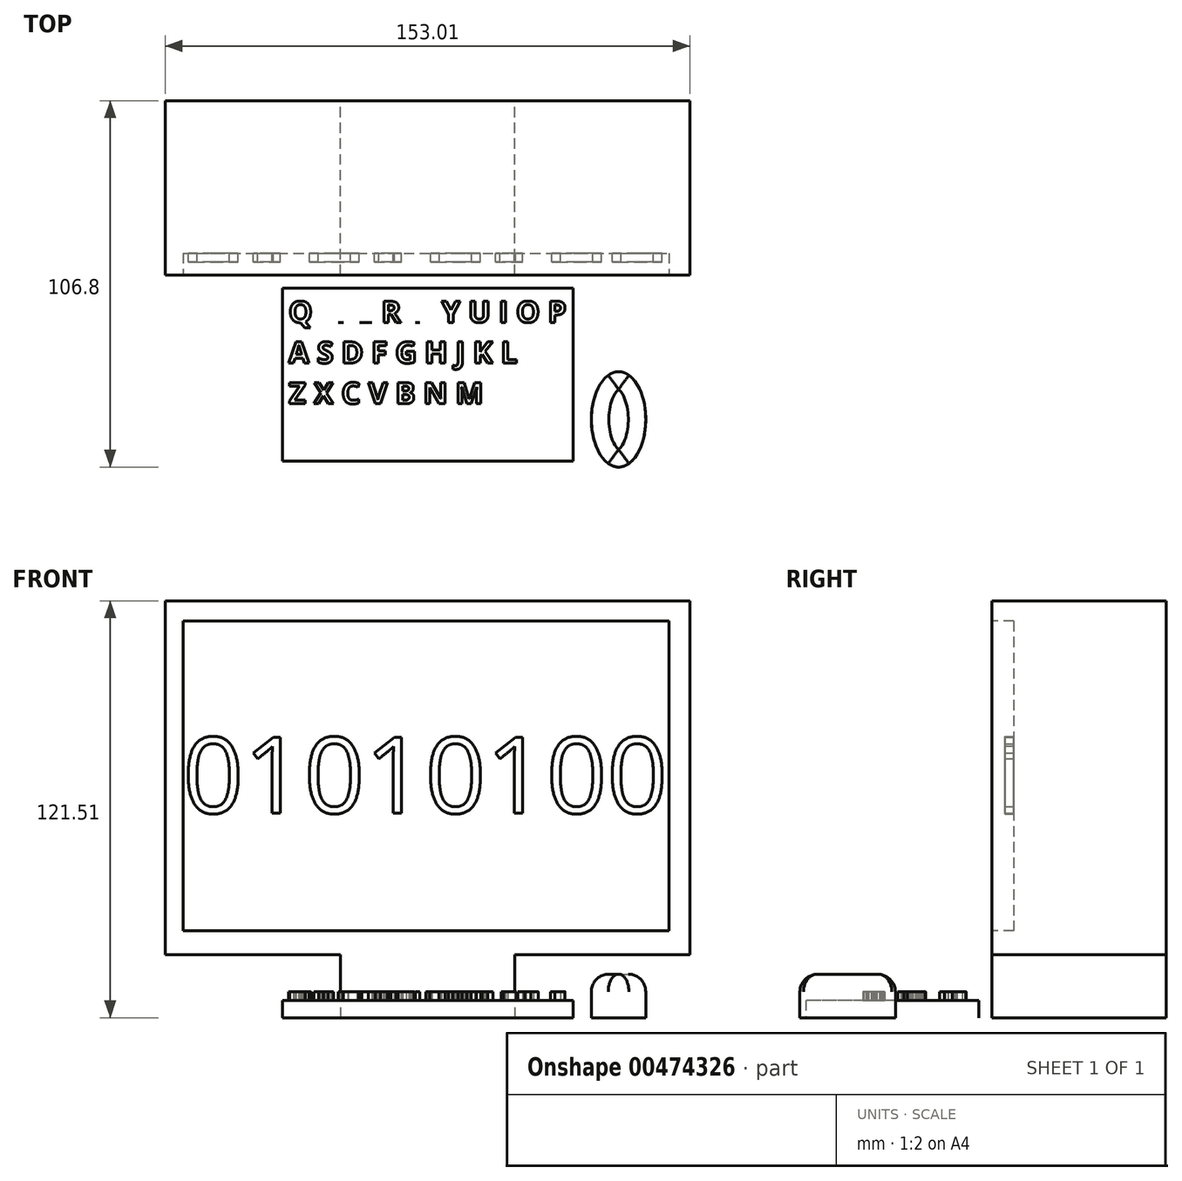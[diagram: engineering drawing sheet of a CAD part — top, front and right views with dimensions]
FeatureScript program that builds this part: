
annotation { "Feature Type Name" : "Feature", "Feature Type Description" : "" }
export const myFeature = defineFeature(function(context is Context, id is Id, definition is map)
    precondition{}
    {
        {
            var Q0;
            Q0=qCreatedBy(makeId("Top.planeOp"),FACE);
            var sketch = newSketch(context, id + "F0", { "sketchPlane" : qUnion([Q0])});
            skLineSegment(sketch, "E0.bottom", {"start": v(25.4, -25.4) * mm, "end": v(-25.4, -25.4) * mm});
            skLineSegment(sketch, "E0.top", {"start": v(25.4, 25.4) * mm, "end": v(-25.4, 25.4) * mm});
            skLineSegment(sketch, "E0.left", {"start": v(25.4, -25.4) * mm, "end": v(25.4, 25.4) * mm});
            skLineSegment(sketch, "E0.right", {"start": v(-25.4, -25.4) * mm, "end": v(-25.4, 25.4) * mm});
            skPoint(sketch, "E0.middle", {"position": v(0, 0) * mm});
            skSolve(sketch);
        }
        {
            var Q0;
            Q0=qSketchRegion(id+"F0",true);
            extrude(context, id + "F1", {"entities" : qUnion([Q0]), "depth" : 25.4 * mm});
        }
        {
            var Q0;
            Q0=qCreatedBy(makeId("Front.planeOp"),FACE);
            var sketch = newSketch(context, id + "F2", { "sketchPlane" : qUnion([Q0])});
            skLineSegment(sketch, "E1.bottom", {"start": v(-76.56, 18.4) * mm, "end": v(76.45, 18.4) * mm});
            skLineSegment(sketch, "E1.top", {"start": v(-76.56, 121.5) * mm, "end": v(76.45, 121.5) * mm});
            skLineSegment(sketch, "E1.left", {"start": v(-76.56, 18.4) * mm, "end": v(-76.56, 121.5) * mm});
            skLineSegment(sketch, "E1.right", {"start": v(76.45, 18.4) * mm, "end": v(76.45, 121.5) * mm});
            skSolve(sketch);
        }
        {
            var Q0;
            Q0=makeQuery(id+"F2.imprint","IMPRINT",FACE,{"disambiguationData":[TD([[makeQuery(id+"F2.imprint","IMPRINT",EDGE,{"derivedFrom":sQuery(id+"F2.wireOp",EDGE,"E1.bottom")}),1.0]])]});
            extrude(context, id + "F3", {"entities" : qUnion([Q0]), "operationType" : NewBodyOperationType.ADD, "depth" : 25.4 * mm});
        }
        {
            var Q0;
            Q0=makeQuery(id+"F3.opExtrude","CAP_FACE",FACE,{"disambiguationData":[OSD([sQuery(id+"F2.wireOp",EDGE,"E1.bottom"),sQuery(id+"F2.wireOp",EDGE,"E1.top"),sQuery(id+"F2.wireOp",EDGE,"E1.left"),sQuery(id+"F2.wireOp",EDGE,"E1.right")])],"isStart":true});
            extrude(context, id + "F4", {"entities" : qUnion([Q0]), "operationType" : NewBodyOperationType.ADD, "depth" : 25.4 * mm});
        }
        {
            var Q0;
            Q0=makeQuery(id+"F3.boolean.opBoolean","MERGE",FACE,{"derivedFrom":[makeQuery(id+"F1.opExtrude","SWEPT_FACE",FACE,{"disambiguationData":[OSD([sQuery(id+"F0.wireOp",EDGE,"E0.bottom")])]}),makeQuery(id+"F3.opExtrude","CAP_FACE",FACE,{"disambiguationData":[OSD([sQuery(id+"F2.wireOp",EDGE,"E1.bottom"),sQuery(id+"F2.wireOp",EDGE,"E1.top"),sQuery(id+"F2.wireOp",EDGE,"E1.left"),sQuery(id+"F2.wireOp",EDGE,"E1.right")])],"isStart":false})]});
            var sketch = newSketch(context, id + "F5", { "sketchPlane" : qUnion([Q0])});
            skLineSegment(sketch, "E2.bottom", {"start": v(-71.36, 115.62) * mm, "end": v(70.34, 115.62) * mm});
            skLineSegment(sketch, "E2.top", {"start": v(-71.36, 25.36) * mm, "end": v(70.34, 25.36) * mm});
            skLineSegment(sketch, "E2.left", {"start": v(-71.36, 115.62) * mm, "end": v(-71.36, 25.36) * mm});
            skLineSegment(sketch, "E2.right", {"start": v(70.34, 115.62) * mm, "end": v(70.34, 25.36) * mm});
            skSolve(sketch);
        }
        {
            var Q0;
            Q0=makeQuery(id+"F5.imprint","IMPRINT",FACE,{"disambiguationData":[TD([[makeQuery(id+"F5.imprint","IMPRINT",EDGE,{"derivedFrom":sQuery(id+"F5.wireOp",EDGE,"E2.bottom")}),-1.0]])]});
            extrude(context, id + "F6", {"entities" : qUnion([Q0]), "operationType" : NewBodyOperationType.REMOVE, "oppositeDirection" : true, "depth" : 6.35 * mm});
        }
        {
            var Q0;
            Q0=qCreatedBy(makeId("Top.planeOp"),FACE);
            var sketch = newSketch(context, id + "F7", { "sketchPlane" : qUnion([Q0])});
            skEllipse(sketch, "E3", {"center": v(55.6, -67.49) * mm, "majorRadius": 13.91 * mm, "minorRadius": 7.91 * mm, "majorAxis": v(0, 1)});
            skSolve(sketch);
        }
        {
            var Q0;
            Q0=makeQuery(id+"F7.imprint","IMPRINT",FACE,{"disambiguationData":[TD([[makeQuery(id+"F7.imprint","IMPRINT",EDGE,{"derivedFrom":sQuery(id+"F7.wireOp",EDGE,"E3")}),1.0]])]});
            var Q1;
            Q1=sQuery(id+"F7.wireOp",EDGE,"E3");
            extrude(context, id + "F8", {"entities" : qUnion([Q0]), "surfaceEntities" : qUnion([Q1]), "depth" : 12.7 * mm});
        }
        {
            var Q0;
            Q0=makeQuery(id+"F8.opExtrude","CAP_EDGE",EDGE,{"disambiguationData":[OSD([sQuery(id+"F7.wireOp",EDGE,"E3")])],"isStart":false});
            fillet(context, id + "F9", {"entities" : qUnion([Q0]), "radius" : 5.08 * mm, "tangentPropagation" : true, "allowEdgeOverflow" : false});
        }
        {
            var Q0;
            Q0=qCreatedBy(makeId("Top.planeOp"),FACE);
            var sketch = newSketch(context, id + "F10", { "sketchPlane" : qUnion([Q0])});
            skLineSegment(sketch, "E4.bottom", {"start": v(-42.31, -29.26) * mm, "end": v(42.31, -29.26) * mm});
            skLineSegment(sketch, "E4.top", {"start": v(-42.31, -79.63) * mm, "end": v(42.31, -79.63) * mm});
            skLineSegment(sketch, "E4.left", {"start": v(-42.31, -29.26) * mm, "end": v(-42.31, -79.63) * mm});
            skLineSegment(sketch, "E4.right", {"start": v(42.31, -29.26) * mm, "end": v(42.31, -79.63) * mm});
            skPoint(sketch, "E4.middle", {"position": v(0, -54.44) * mm});
            skSolve(sketch);
        }
        {
            var Q0;
            Q0=makeQuery(id+"F10.imprint","IMPRINT",FACE,{"disambiguationData":[TD([[makeQuery(id+"F10.imprint","IMPRINT",EDGE,{"derivedFrom":sQuery(id+"F10.wireOp",EDGE,"E4.bottom")}),-1.0]])]});
            extrude(context, id + "F11", {"entities" : qUnion([Q0]), "depth" : 5.08 * mm});
        }
        {
            var Q0;
            Q0=makeQuery(id+"F11.opExtrude","CAP_FACE",FACE,{"disambiguationData":[OSD([sQuery(id+"F10.wireOp",EDGE,"E4.bottom"),sQuery(id+"F10.wireOp",EDGE,"E4.top"),sQuery(id+"F10.wireOp",EDGE,"E4.left"),sQuery(id+"F10.wireOp",EDGE,"E4.right")])],"isStart":false});
            var sketch = newSketch(context, id + "F12", { "sketchPlane" : qUnion([Q0])});
            skLineSegment(sketch, "E5.bottom", {"start": v(-40.56, -32.99) * mm, "end": v(40.56, -32.99) * mm});
            skLineSegment(sketch, "E5.top", {"start": v(-40.56, -39.26) * mm, "end": v(40.56, -39.26) * mm});
            skLineSegment(sketch, "E5.left", {"start": v(-40.56, -32.99) * mm, "end": v(-40.56, -39.26) * mm});
            skLineSegment(sketch, "E5.right", {"start": v(40.56, -32.99) * mm, "end": v(40.56, -39.26) * mm});
            skPoint(sketch, "E5.middle", {"position": v(0, -36.12) * mm});
            skText(sketch, "E6", { "text": "Q W E R T  Y U I O P\nA S D F G H J K L\nZ X C V B N M", "fontName": "OpenSans-Bold.ttf"});
            const initialGuessF12  = {"E6": [-0.04056, -0.03926, 1, 0, 0.00627]};
            skSetInitialGuess(sketch, initialGuessF12);
            skSolve(sketch);
        }
        {
            var Q0;
            Q0=makeQuery(id+"F12.imprint","IMPRINT",FACE,{"disambiguationData":[TD([[makeQuery(id+"F12.imprint","IMPRINT",EDGE,{"derivedFrom":sQuery(id+"F12.wireOp",EDGE,"E6.sketch_text.stroke-139")}),-1.0]])]});
            var Q1;
            Q1=makeQuery(id+"F12.imprint","IMPRINT",FACE,{"disambiguationData":[TD([[makeQuery(id+"F12.imprint","IMPRINT",EDGE,{"derivedFrom":sQuery(id+"F12.wireOp",EDGE,"E6.sketch_text.stroke-151")}),-1.0]])]});
            var Q2;
            Q2=makeQuery(id+"F12.imprint","IMPRINT",FACE,{"disambiguationData":[TD([[makeQuery(id+"F12.imprint","IMPRINT",EDGE,{"derivedFrom":sQuery(id+"F12.wireOp",EDGE,"E6.sketch_text.stroke-179")}),-1.0]])]});
            var Q3;
            Q3=makeQuery(id+"F12.imprint","IMPRINT",FACE,{"disambiguationData":[TD([[makeQuery(id+"F12.imprint","IMPRINT",EDGE,{"derivedFrom":sQuery(id+"F12.wireOp",EDGE,"E6.sketch_text.stroke-191")}),-1.0]])]});
            var Q4;
            Q4=makeQuery(id+"F12.imprint","IMPRINT",FACE,{"disambiguationData":[TD([[makeQuery(id+"F12.imprint","IMPRINT",EDGE,{"derivedFrom":sQuery(id+"F12.wireOp",EDGE,"E6.sketch_text.stroke-201")}),-1.0]])]});
            var Q5;
            Q5=makeQuery(id+"F12.imprint","IMPRINT",FACE,{"disambiguationData":[TD([[makeQuery(id+"F12.imprint","IMPRINT",EDGE,{"derivedFrom":sQuery(id+"F12.wireOp",EDGE,"E6.sketch_text.stroke-220")}),-1.0]])]});
            var Q6;
            Q6=makeQuery(id+"F12.imprint","IMPRINT",FACE,{"disambiguationData":[TD([[makeQuery(id+"F12.imprint","IMPRINT",EDGE,{"derivedFrom":sQuery(id+"F12.wireOp",EDGE,"E6.sketch_text.stroke-232")}),-1.0]])]});
            var Q7;
            Q7=makeQuery(id+"F12.imprint","IMPRINT",FACE,{"disambiguationData":[TD([[makeQuery(id+"F12.imprint","IMPRINT",EDGE,{"derivedFrom":sQuery(id+"F12.wireOp",EDGE,"E6.sketch_text.stroke-242")}),-1.0]])]});
            var Q8;
            Q8=makeQuery(id+"F12.imprint","IMPRINT",FACE,{"disambiguationData":[TD([[makeQuery(id+"F12.imprint","IMPRINT",EDGE,{"derivedFrom":sQuery(id+"F12.wireOp",EDGE,"E6.sketch_text.stroke-255")}),-1.0]])]});
            extrude(context, id + "F13", {"entities" : qUnion([Q0, Q1, Q2, Q3, Q4, Q5, Q6, Q7, Q8]), "operationType" : NewBodyOperationType.ADD, "depth" : 2.54 * mm});
        }
        {
            var Q0;
            Q0=makeQuery(id+"F12.imprint","IMPRINT",FACE,{"disambiguationData":[TD([[makeQuery(id+"F12.imprint","IMPRINT",EDGE,{"derivedFrom":sQuery(id+"F12.wireOp",EDGE,"E6.sketch_text.stroke-123")}),-1.0]])]});
            var Q1;
            {var subQ11=sQuery(id+"F12.wireOp",EDGE,"E6.sketch_text.stroke-109");Q1=makeQuery(id+"F12.imprint","IMPRINT",FACE,{"disambiguationData":[TD([[makeQuery(id+"F12.imprint","IMPRINT",EDGE,{"derivedFrom":subQ11}),-1.0]])]});}
            var Q2;
            Q2=makeQuery(id+"F12.imprint","IMPRINT",FACE,{"disambiguationData":[TD([[makeQuery(id+"F12.imprint","IMPRINT",EDGE,{"derivedFrom":sQuery(id+"F12.wireOp",EDGE,"E6.sketch_text.stroke-105")}),-1.0]])]});
            var Q3;
            Q3=makeQuery(id+"F12.imprint","IMPRINT",FACE,{"disambiguationData":[TD([[makeQuery(id+"F12.imprint","IMPRINT",EDGE,{"derivedFrom":sQuery(id+"F12.wireOp",EDGE,"E6.sketch_text.stroke-90")}),-1.0]])]});
            var Q4;
            Q4=makeQuery(id+"F12.imprint","IMPRINT",FACE,{"disambiguationData":[TD([[makeQuery(id+"F12.imprint","IMPRINT",EDGE,{"derivedFrom":sQuery(id+"F12.wireOp",EDGE,"E6.sketch_text.stroke-81")}),-1.0]])]});
            var Q5;
            Q5=makeQuery(id+"F12.imprint","IMPRINT",FACE,{"disambiguationData":[TD([[makeQuery(id+"F12.imprint","IMPRINT",EDGE,{"derivedFrom":sQuery(id+"F12.wireOp",EDGE,"E6.sketch_text.stroke-73")}),-1.0]])]});
            var Q6;
            Q6=makeQuery(id+"F12.imprint","IMPRINT",FACE,{"disambiguationData":[TD([[makeQuery(id+"F12.imprint","IMPRINT",EDGE,{"derivedFrom":sQuery(id+"F12.wireOp",EDGE,"E6.sketch_text.stroke-54")}),-1.0]])]});
            var Q7;
            Q7=makeQuery(id+"F12.imprint","IMPRINT",FACE,{"disambiguationData":[TD([[makeQuery(id+"F12.imprint","IMPRINT",EDGE,{"derivedFrom":sQuery(id+"F12.wireOp",EDGE,"E6.sketch_text.stroke-42")}),-1.0]])]});
            var Q8;
            Q8=makeQuery(id+"F12.imprint","IMPRINT",FACE,{"disambiguationData":[TD([[makeQuery(id+"F12.imprint","IMPRINT",EDGE,{"derivedFrom":sQuery(id+"F12.wireOp",EDGE,"E6.sketch_text.stroke-18")}),-1.0]])]});
            var Q9;
            Q9=makeQuery(id+"F12.imprint","IMPRINT",FACE,{"disambiguationData":[TD([[makeQuery(id+"F12.imprint","IMPRINT",EDGE,{"derivedFrom":sQuery(id+"F12.wireOp",EDGE,"E6.sketch_text.stroke-0")}),-1.0]])]});
            var Q10;
            {var subQ5=sQuery(id+"F12.wireOp",EDGE,"E6.sketch_text.stroke-3");Q10=makeQuery(id+"F12.imprint","IMPRINT",FACE,{"disambiguationData":[TD([[makeQuery(id+"F12.imprint","IMPRINT",EDGE,{"derivedFrom":subQ5}),-1.0]])]});}
            extrude(context, id + "F14", {"entities" : qUnion([Q0, Q1, Q2, Q3, Q4, Q5, Q6, Q7, Q8, Q9, Q10]), "operationType" : NewBodyOperationType.ADD, "depth" : 2.54 * mm});
        }
        {
            var Q0;
            Q0=makeQuery(id+"F12.imprint","IMPRINT",FACE,{"disambiguationData":[TD([[makeQuery(id+"F12.imprint","IMPRINT",EDGE,{"derivedFrom":sQuery(id+"F12.wireOp",EDGE,"E6.sketch_text.stroke-261")}),-1.0]])]});
            var Q1;
            Q1=makeQuery(id+"F12.imprint","IMPRINT",FACE,{"disambiguationData":[TD([[makeQuery(id+"F12.imprint","IMPRINT",EDGE,{"derivedFrom":sQuery(id+"F12.wireOp",EDGE,"E6.sketch_text.stroke-271")}),-1.0]])]});
            var Q2;
            Q2=makeQuery(id+"F12.imprint","IMPRINT",FACE,{"disambiguationData":[TD([[makeQuery(id+"F12.imprint","IMPRINT",EDGE,{"derivedFrom":sQuery(id+"F12.wireOp",EDGE,"E6.sketch_text.stroke-283")}),-1.0]])]});
            var Q3;
            Q3=makeQuery(id+"F12.imprint","IMPRINT",FACE,{"disambiguationData":[TD([[makeQuery(id+"F12.imprint","IMPRINT",EDGE,{"derivedFrom":sQuery(id+"F12.wireOp",EDGE,"E6.sketch_text.stroke-298")}),-1.0]])]});
            var Q4;
            Q4=makeQuery(id+"F12.imprint","IMPRINT",FACE,{"disambiguationData":[TD([[makeQuery(id+"F12.imprint","IMPRINT",EDGE,{"derivedFrom":sQuery(id+"F12.wireOp",EDGE,"E6.sketch_text.stroke-308")}),-1.0]])]});
            var Q5;
            Q5=makeQuery(id+"F12.imprint","IMPRINT",FACE,{"disambiguationData":[TD([[makeQuery(id+"F12.imprint","IMPRINT",EDGE,{"derivedFrom":sQuery(id+"F12.wireOp",EDGE,"E6.sketch_text.stroke-333")}),-1.0]])]});
            var Q6;
            Q6=makeQuery(id+"F12.imprint","IMPRINT",FACE,{"disambiguationData":[TD([[makeQuery(id+"F12.imprint","IMPRINT",EDGE,{"derivedFrom":sQuery(id+"F12.wireOp",EDGE,"E6.sketch_text.stroke-347")}),-1.0]])]});
            extrude(context, id + "F15", {"entities" : qUnion([Q0, Q1, Q2, Q3, Q4, Q5, Q6]), "operationType" : NewBodyOperationType.ADD, "depth" : 2.54 * mm});
        }
        {
            var Q0;
            Q0=makeQuery(id+"F6.boolean.opBoolean","COPY",FACE,{"derivedFrom":makeQuery(id+"F6.opExtrude","CAP_FACE",FACE,{"disambiguationData":[OSD([sQuery(id+"F5.wireOp",EDGE,"E2.bottom"),sQuery(id+"F5.wireOp",EDGE,"E2.top"),sQuery(id+"F5.wireOp",EDGE,"E2.left"),sQuery(id+"F5.wireOp",EDGE,"E2.right")])],"isStart":false})});
            var sketch = newSketch(context, id + "F16", { "sketchPlane" : qUnion([Q0])});
            skText(sketch, "E7", { "text": "01010100", "fontName": "OpenSans-Regular.ttf"});
            const initialGuessF16  = {"E7": [-0.07136, 0.05964, 1, 0, 0.02223]};
            skSetInitialGuess(sketch, initialGuessF16);
            skSolve(sketch);
        }
        {
            var Q0;
            Q0=makeQuery(id+"F16.imprint","IMPRINT",FACE,{"disambiguationData":[TD([[makeQuery(id+"F16.imprint","IMPRINT",EDGE,{"derivedFrom":sQuery(id+"F16.wireOp",EDGE,"E7.sketch_text.stroke-0")}),-1.0]])]});
            var Q1;
            Q1=makeQuery(id+"F16.imprint","IMPRINT",FACE,{"disambiguationData":[TD([[makeQuery(id+"F16.imprint","IMPRINT",EDGE,{"derivedFrom":sQuery(id+"F16.wireOp",EDGE,"E7.sketch_text.stroke-16")}),-1.0]])]});
            var Q2;
            Q2=makeQuery(id+"F16.imprint","IMPRINT",FACE,{"disambiguationData":[TD([[makeQuery(id+"F16.imprint","IMPRINT",EDGE,{"derivedFrom":sQuery(id+"F16.wireOp",EDGE,"E7.sketch_text.stroke-25")}),-1.0]])]});
            var Q3;
            Q3=makeQuery(id+"F16.imprint","IMPRINT",FACE,{"disambiguationData":[TD([[makeQuery(id+"F16.imprint","IMPRINT",EDGE,{"derivedFrom":sQuery(id+"F16.wireOp",EDGE,"E7.sketch_text.stroke-41")}),-1.0]])]});
            var Q4;
            Q4=makeQuery(id+"F16.imprint","IMPRINT",FACE,{"disambiguationData":[TD([[makeQuery(id+"F16.imprint","IMPRINT",EDGE,{"derivedFrom":sQuery(id+"F16.wireOp",EDGE,"E7.sketch_text.stroke-50")}),-1.0]])]});
            var Q5;
            Q5=makeQuery(id+"F16.imprint","IMPRINT",FACE,{"disambiguationData":[TD([[makeQuery(id+"F16.imprint","IMPRINT",EDGE,{"derivedFrom":sQuery(id+"F16.wireOp",EDGE,"E7.sketch_text.stroke-66")}),-1.0]])]});
            var Q6;
            Q6=makeQuery(id+"F16.imprint","IMPRINT",FACE,{"disambiguationData":[TD([[makeQuery(id+"F16.imprint","IMPRINT",EDGE,{"derivedFrom":sQuery(id+"F16.wireOp",EDGE,"E7.sketch_text.stroke-75")}),-1.0]])]});
            var Q7;
            Q7=makeQuery(id+"F16.imprint","IMPRINT",FACE,{"disambiguationData":[TD([[makeQuery(id+"F16.imprint","IMPRINT",EDGE,{"derivedFrom":sQuery(id+"F16.wireOp",EDGE,"E7.sketch_text.stroke-91")}),-1.0]])]});
            extrude(context, id + "F17", {"entities" : qUnion([Q0, Q1, Q2, Q3, Q4, Q5, Q6, Q7]), "operationType" : NewBodyOperationType.ADD, "depth" : 2.54 * mm});
        }
    });
